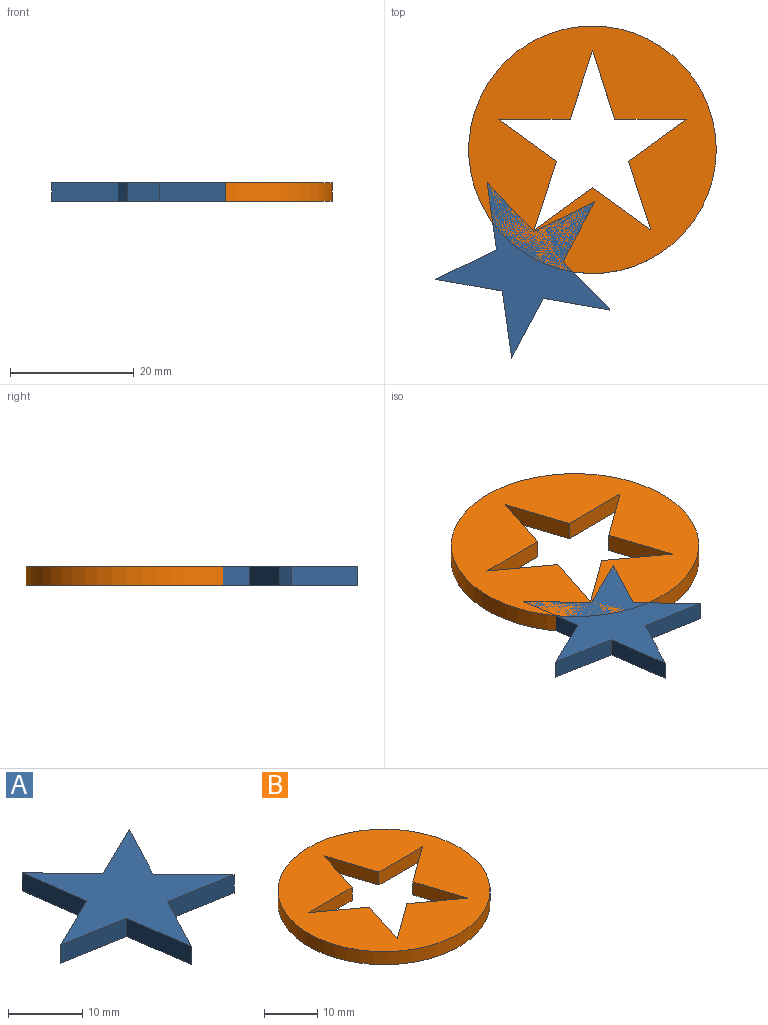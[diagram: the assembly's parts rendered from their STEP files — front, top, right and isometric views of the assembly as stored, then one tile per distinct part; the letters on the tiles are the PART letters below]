
ASSEMBLY  parts=2 mates=1
PART A: 12 faces, bbox 28.2x28.3x3 mm
  f0: plane 9.64x5.12mm, normal (0.88,-0.47,0), area 32.8mm2, adj f1,f9,f10,f11
  f1: plane 10.75x3mm, normal (-0.17,-0.98,0), area 32.8mm2, adj f0,f2,f10,f11
  f2: plane 7.85x7.59mm, normal (0.72,0.69,0), area 32.8mm2, adj f1,f3,f10,f11
  f3: plane 9.64x5.12mm, normal (0.88,-0.47,0), area 32.8mm2, adj f2,f4,f10,f11
  f4: plane 9.81x4.79mm, normal (-0.44,0.9,0), area 32.8mm2, adj f3,f5,f10,f11
  f5: plane 7.85x7.59mm, normal (0.72,0.69,0), area 32.8mm2, adj f4,f6,f10,f11
  f6: plane 10.81x3mm, normal (-0.99,-0.14,0), area 32.8mm2, adj f5,f7,f10,f11
  f7: plane 9.81x4.79mm, normal (-0.44,0.9,0), area 32.8mm2, adj f6,f8,f10,f11
  f8: plane 10.75x3mm, normal (-0.17,-0.98,0), area 32.8mm2, adj f7,f9,f10,f11
  f9: plane 10.81x3mm, normal (-0.99,-0.14,0), area 32.8mm2, adj f0,f8,f10,f11
  f10: plane 28.31x28.15mm, normal (0,0,1), area 253.6mm2, adj f0,f1,f2,f3,f4,f5,f6,f7
  f11: plane 28.31x28.15mm, normal (0,0,-1), area 253.6mm2, adj f0,f1,f2,f3,f4,f5,f6,f7
PART B: 13 faces, bbox 40x40x3 mm
  f0: cylinder r=20mm len=40mm, axis (0,0,-1), area 377mm2, adj f1,f2
  f1: plane 40x40mm, normal (0,0,1), area 969.3mm2, adj f0,f3,f4,f5,f6,f7,f8,f9
  f2: plane 40x40mm, normal (0,0,-1), area 969.3mm2, adj f0,f3,f4,f5,f6,f7,f8,f9
  f3: plane 9.4x6.83mm, normal (0.59,0.81,0), area 34.9mm2, adj f1,f2,f4,f12
  f4: plane 11.06x3.59mm, normal (-0.95,-0.31,0), area 34.9mm2, adj f1,f2,f3,f5
  f5: plane 9.4x6.83mm, normal (-0.59,0.81,0), area 34.9mm2, adj f1,f2,f4,f6
  f6: plane 11.62x3mm, normal (0,-1,0), area 34.9mm2, adj f1,f2,f5,f7
  f7: plane 11.06x3.59mm, normal (-0.95,-0.31,0), area 34.9mm2, adj f1,f2,f6,f8
  f8: plane 11.06x3.59mm, normal (0.95,-0.31,0), area 34.9mm2, adj f1,f2,f7,f9
  f9: plane 11.62x3mm, normal (0,-1,0), area 34.9mm2, adj f1,f2,f8,f10
  f10: plane 9.4x6.83mm, normal (0.59,0.81,0), area 34.9mm2, adj f1,f2,f9,f11
  f11: plane 11.06x3.59mm, normal (0.95,-0.31,0), area 34.9mm2, adj f1,f2,f10,f12
  f12: plane 9.4x6.83mm, normal (-0.59,0.81,0), area 34.9mm2, adj f1,f2,f3,f11
PLACE A t=(-13.06,-19.91,11.29)mm
PLACE B t=(-2.62,-1.07,11.29)mm
MATE parallel A.f11 <-> B.f2  axis (0,0,-1) through (-12.07,-14.25,11.29)mm
